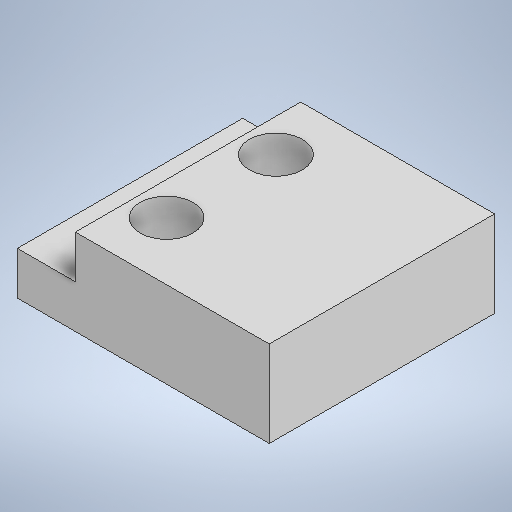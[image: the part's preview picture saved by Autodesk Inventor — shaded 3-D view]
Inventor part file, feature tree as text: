
AUTODESK INVENTOR PART (.ipt)
format: ipt  version: 2025.1 (Build 291241000, 241)  size: 228,864 bytes
history: native  units: in
note: dims shown in document units (in); Inventor stores cm internally (conversion verified against a paired STEP export)
features: extrude x2, sketch x2
ambient origin geometry x8: Origin, YZ Plane, XZ Plane, XY Plane, X Axis, Y Axis, Z Axis, Center Point
bodies: Solid1 (feature_tree)
feature tree (4):
  extrude  "Extrusion1"  Depth=0.5984in
  extrude  "Extrusion3"  Depth=0.1378in
  sketch  "Sketch1"  dims[d0=0.5354in d1=0.5984in]
  sketch  "Sketch2"  dims[d2=0.126in d3=0.1378in d4=0.1378in d5=0.2165in d7=0.1024in d8=0.0in d9=0.1378in d12=0.1024in d13=0.0in]
